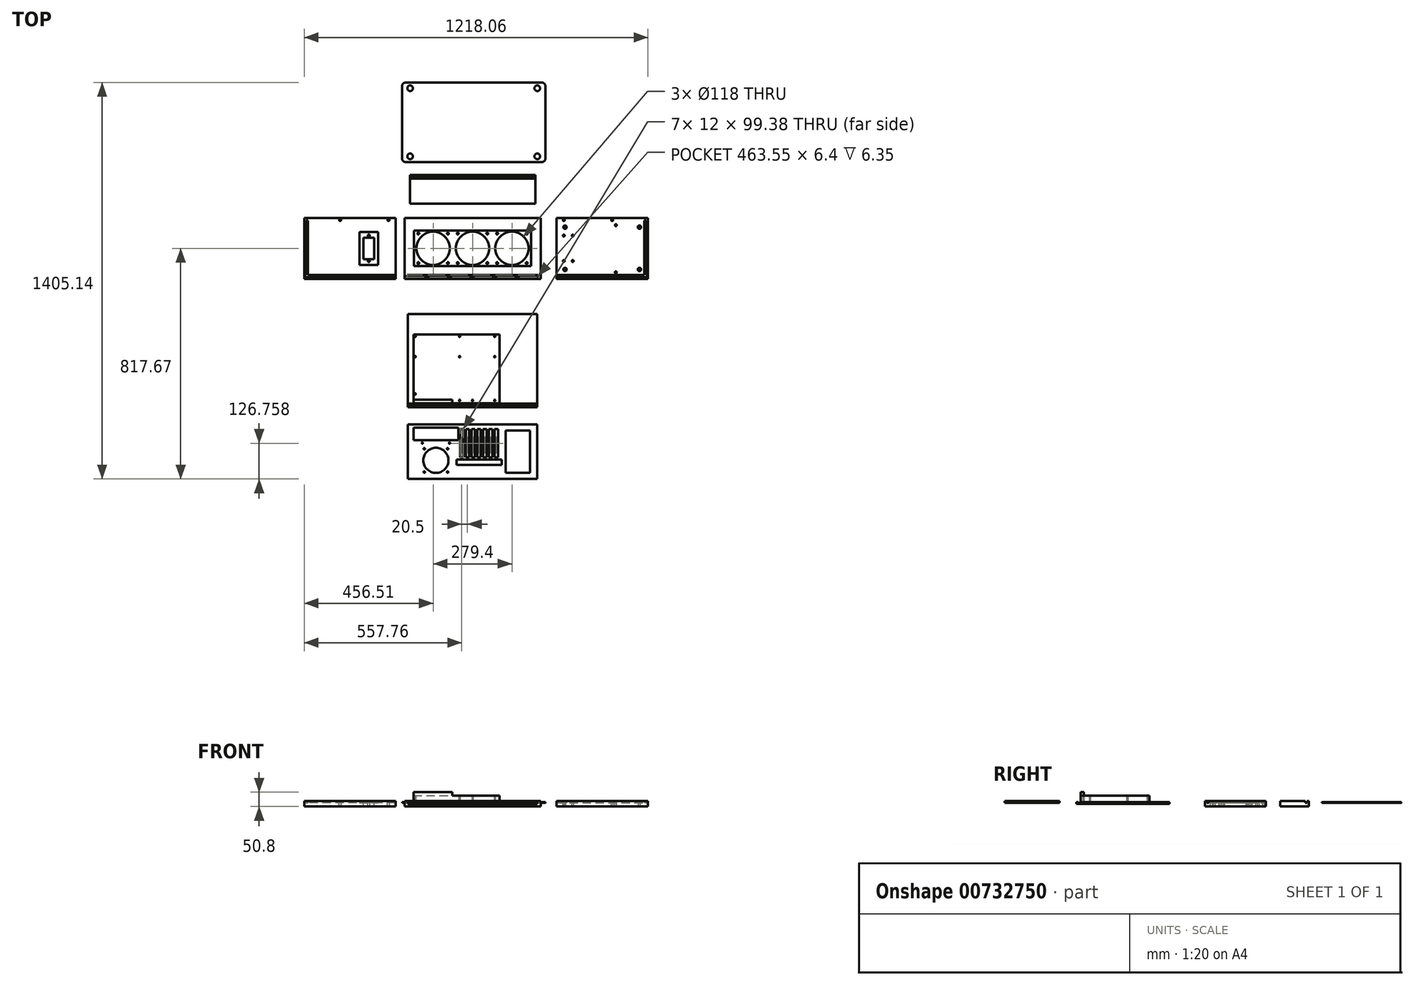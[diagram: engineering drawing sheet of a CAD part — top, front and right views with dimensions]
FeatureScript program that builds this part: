
annotation { "Feature Type Name" : "Feature", "Feature Type Description" : "" }
export const myFeature = defineFeature(function(context is Context, id is Id, definition is map)
    precondition{}
    {
        {
            var Q0;
            Q0=qCreatedBy(makeId("Top.planeOp"),FACE);
            var sketch = newSketch(context, id + "F0", { "sketchPlane" : qUnion([Q0])});
            skLineSegment(sketch, "E0.bottom", {"start": v(241.3, -107.95) * mm, "end": v(-241.3, -107.95) * mm});
            skLineSegment(sketch, "E0.top", {"start": v(241.3, 107.95) * mm, "end": v(-241.3, 107.95) * mm});
            skLineSegment(sketch, "E0.left", {"start": v(241.3, -107.95) * mm, "end": v(241.3, 107.95) * mm});
            skLineSegment(sketch, "E0.right", {"start": v(-241.3, -107.95) * mm, "end": v(-241.3, 107.95) * mm});
            skPoint(sketch, "E0.middle", {"position": v(0, 0) * mm});
            skLineSegment(sketch, "E1.bottom", {"start": v(231.78, -101.6) * mm, "end": v(-231.78, -101.6) * mm});
            skLineSegment(sketch, "E1.top", {"start": v(231.78, -95.2) * mm, "end": v(-231.78, -95.2) * mm});
            skLineSegment(sketch, "E1.left", {"start": v(231.78, -101.6) * mm, "end": v(231.78, -95.2) * mm});
            skLineSegment(sketch, "E1.right", {"start": v(-231.78, -101.6) * mm, "end": v(-231.78, -95.2) * mm});
            skPoint(sketch, "E1.middle", {"position": v(0, -98.4) * mm});
            skCircle(sketch, "E2", {"center": v(139.7, 0) * mm, "radius": 59 * mm});
            skCircle(sketch, "E3", {"center": v(-139.7, 0) * mm, "radius": 59 * mm});
            skCircle(sketch, "E4", {"center": v(0, 0) * mm, "radius": 59 * mm});
            skCircle(sketch, "E5", {"center": v(-192.2, 52.5) * mm, "radius": 3.19 * mm});
            skCircle(sketch, "E6", {"center": v(-192.2, -52.5) * mm, "radius": 3.19 * mm});
            skCircle(sketch, "E7", {"center": v(-87.2, -52.5) * mm, "radius": 3.19 * mm});
            skCircle(sketch, "E8", {"center": v(-87.2, 52.5) * mm, "radius": 3.19 * mm});
            skCircle(sketch, "E9", {"center": v(-52.5, 52.5) * mm, "radius": 3.19 * mm});
            skCircle(sketch, "E10", {"center": v(52.5, 52.5) * mm, "radius": 3.19 * mm});
            skCircle(sketch, "E11", {"center": v(-52.5, -52.5) * mm, "radius": 3.19 * mm});
            skCircle(sketch, "E12", {"center": v(52.5, -52.5) * mm, "radius": 3.19 * mm});
            skCircle(sketch, "E13", {"center": v(87.2, -52.5) * mm, "radius": 3.19 * mm});
            skCircle(sketch, "E14", {"center": v(87.2, 52.5) * mm, "radius": 3.19 * mm});
            skCircle(sketch, "E15", {"center": v(192.2, 52.5) * mm, "radius": 3.19 * mm});
            skCircle(sketch, "E16", {"center": v(192.2, -52.5) * mm, "radius": 3.19 * mm});
            skLineSegment(sketch, "E17.bottom", {"start": v(207.17, -62.5) * mm, "end": v(-207.17, -62.5) * mm});
            skLineSegment(sketch, "E17.top", {"start": v(207.17, 62.5) * mm, "end": v(-207.17, 62.5) * mm});
            skLineSegment(sketch, "E17.left", {"start": v(207.17, -62.5) * mm, "end": v(207.17, 62.5) * mm});
            skLineSegment(sketch, "E17.right", {"start": v(-207.17, -62.5) * mm, "end": v(-207.17, 62.5) * mm});
            skSolve(sketch);
        }
        {
            var Q0;
            Q0=makeQuery(id+"F0.imprint","IMPRINT",FACE,{"disambiguationData":[TD([[makeQuery(id+"F0.imprint","IMPRINT",EDGE,{"derivedFrom":sQuery(id+"F0.wireOp",EDGE,"E1.bottom")}),-1.0]])]});
            var Q1;
            Q1=makeQuery(id+"F0.imprint","IMPRINT",FACE,{"disambiguationData":[TD([[makeQuery(id+"F0.imprint","IMPRINT",EDGE,{"derivedFrom":sQuery(id+"F0.wireOp",EDGE,"E0.bottom")}),-1.0]])]});
            var Q2;
            Q2=makeQuery(id+"F0.imprint","IMPRINT",FACE,{"disambiguationData":[TD([[makeQuery(id+"F0.imprint","IMPRINT",EDGE,{"derivedFrom":sQuery(id+"F0.wireOp",EDGE,"E2")}),-1.0]])]});
            extrude(context, id + "F1", {"entities" : qUnion([Q0, Q1, Q2]), "oppositeDirection" : true, "depth" : 12.7 * mm, "offsetDistance" : 25.4 * mm});
        }
        {
            var Q0;
            Q0=makeQuery(id+"F0.imprint","IMPRINT",FACE,{"disambiguationData":[TD([[makeQuery(id+"F0.imprint","IMPRINT",EDGE,{"derivedFrom":sQuery(id+"F0.wireOp",EDGE,"E0.bottom")}),-1.0]])]});
            extrude(context, id + "F2", {"entities" : qUnion([Q0]), "operationType" : NewBodyOperationType.ADD, "depth" : 6.35 * mm, "offsetDistance" : 25.4 * mm});
        }
        {
            var Q0;
            Q0=qCreatedBy(makeId("Top.planeOp"),FACE);
            var sketch = newSketch(context, id + "F3", { "sketchPlane" : qUnion([Q0])});
            skPoint(sketch, "E18.0", {"position": v(231.78, -95.2) * mm});
            skPoint(sketch, "E18.1", {"position": v(231.78, -101.6) * mm});
            skPoint(sketch, "E18.2", {"position": v(241.3, -107.95) * mm});
            skPoint(sketch, "E18.3", {"position": v(241.3, 107.95) * mm});
            skLineSegment(sketch, "E19.bottom", {"start": v(298, -107.95) * mm, "end": v(621.85, -107.95) * mm});
            skLineSegment(sketch, "E19.top", {"start": v(298, 107.95) * mm, "end": v(621.85, 107.95) * mm});
            skLineSegment(sketch, "E19.left", {"start": v(298, -107.95) * mm, "end": v(298, 107.95) * mm});
            skLineSegment(sketch, "E19.right", {"start": v(621.85, -107.95) * mm, "end": v(621.85, 107.95) * mm});
            skPoint(sketch, "E19.middle", {"position": v(459.93, 0) * mm});
            skLineSegment(sketch, "E20.bottom", {"start": v(294.83, -95.2) * mm, "end": v(625.03, -95.2) * mm});
            skLineSegment(sketch, "E20.top", {"start": v(294.83, -101.6) * mm, "end": v(625.03, -101.6) * mm});
            skLineSegment(sketch, "E20.left", {"start": v(294.83, -95.2) * mm, "end": v(294.83, -101.6) * mm});
            skLineSegment(sketch, "E20.right", {"start": v(625.03, -95.2) * mm, "end": v(625.03, -101.6) * mm});
            skLineSegment(sketch, "E21.bottom", {"start": v(615.5, -97.9) * mm, "end": v(609.13, -97.9) * mm});
            skLineSegment(sketch, "E21.top", {"start": v(615.5, 98.43) * mm, "end": v(609.13, 98.43) * mm});
            skLineSegment(sketch, "E21.left", {"start": v(615.5, -97.9) * mm, "end": v(615.5, 98.43) * mm});
            skLineSegment(sketch, "E21.right", {"start": v(609.13, -97.9) * mm, "end": v(609.13, 98.43) * mm});
            skCircle(sketch, "E22", {"center": v(328, 74.95) * mm, "radius": 3.3 * mm});
            skCircle(sketch, "E23", {"center": v(328, -74.95) * mm, "radius": 3.3 * mm});
            skCircle(sketch, "E24", {"center": v(591.85, -74.95) * mm, "radius": 3.3 * mm});
            skCircle(sketch, "E25", {"center": v(591.85, 74.95) * mm, "radius": 3.3 * mm});
            skCircle(sketch, "E26", {"center": v(328, 74.95) * mm, "radius": 6 * mm});
            skCircle(sketch, "E27", {"center": v(328, -74.95) * mm, "radius": 6 * mm});
            skCircle(sketch, "E28", {"center": v(591.85, 74.95) * mm, "radius": 6 * mm});
            skCircle(sketch, "E29", {"center": v(591.85, -74.95) * mm, "radius": 6 * mm});
            skPoint(sketch, "E30", {"position": v(520.25, -20.34) * mm});
            skCircle(sketch, "E31", {"center": v(494.85, 99.95) * mm, "radius": 3.3 * mm});
            skCircle(sketch, "E32", {"center": v(323.4, 99.95) * mm, "radius": 3.3 * mm});
            skPoint(sketch, "E33.centerSnap0", {"position": v(298, 0) * mm});
            skCircle(sketch, "E34", {"center": v(508.13, 81.95) * mm, "radius": 3.3 * mm});
            skCircle(sketch, "E35", {"center": v(508.13, -85.4) * mm, "radius": 3.3 * mm});
            skLineSegment(sketch, "E36.bottom", {"start": v(355.2, -45.09) * mm, "end": v(323.4, -45.09) * mm});
            skLineSegment(sketch, "E36.top", {"start": v(355.2, 45.08) * mm, "end": v(323.4, 45.08) * mm});
            skLineSegment(sketch, "E36.left", {"start": v(355.2, -45.09) * mm, "end": v(355.2, 45.08) * mm});
            skLineSegment(sketch, "E36.right", {"start": v(323.4, -45.09) * mm, "end": v(323.4, 45.08) * mm});
            skPoint(sketch, "E36.middle", {"position": v(339.3, 0) * mm});
            skCircle(sketch, "E37", {"center": v(323.4, 45.08) * mm, "radius": 3.3 * mm});
            skCircle(sketch, "E38", {"center": v(355.2, 45.08) * mm, "radius": 3.3 * mm});
            skCircle(sketch, "E39", {"center": v(323.4, -45.09) * mm, "radius": 3.3 * mm});
            skCircle(sketch, "E40", {"center": v(355.2, -45.09) * mm, "radius": 3.3 * mm});
            skSolve(sketch);
        }
        {
            var Q0;
            {var subQ0=sQuery(id+"F3.wireOp",EDGE,"E19.left");var subQ1=sQuery(id+"F3.wireOp",EDGE,"E19.top");var subQ2=makeQuery(id+"F3.imprint","INTERSECT",VERTEX,{"derivedFrom":[subQ1,subQ0]});Q0=makeQuery(id+"F3.imprint","IMPRINT",FACE,{"disambiguationData":[TD([[makeQuery(id+"F3.imprint","IMPRINT",EDGE,{"disambiguationData":[TD([[subQ2,-1.0]])],"derivedFrom":subQ1}),-1.0]])]});}
            var Q1;
            {var subQ0=sQuery(id+"F3.wireOp",EDGE,"E21.right");var subQ1=sQuery(id+"F3.wireOp",EDGE,"E19.top");var subQ2=makeQuery(id+"F3.imprint","INTERSECT",VERTEX,{"derivedFrom":[subQ1,subQ0]});Q1=makeQuery(id+"F3.imprint","IMPRINT",FACE,{"disambiguationData":[TD([[makeQuery(id+"F3.imprint","IMPRINT",EDGE,{"disambiguationData":[TD([[subQ2,-1.0]])],"derivedFrom":subQ1}),-1.0]])]});}
            var Q2;
            {var subQ0=sQuery(id+"F3.wireOp",EDGE,"E19.right");var subQ1=sQuery(id+"F3.wireOp",EDGE,"E19.top");var subQ2=makeQuery(id+"F3.imprint","INTERSECT",VERTEX,{"derivedFrom":[subQ1,subQ0]});Q2=makeQuery(id+"F3.imprint","IMPRINT",FACE,{"disambiguationData":[TD([[makeQuery(id+"F3.imprint","IMPRINT",EDGE,{"disambiguationData":[TD([[subQ2,1.0]])],"derivedFrom":subQ1}),-1.0]])]});}
            var Q3;
            {var subQ6=sQuery(id+"F3.wireOp",EDGE,"E21.bottom");Q3=makeQuery(id+"F3.imprint","IMPRINT",FACE,{"disambiguationData":[TD([[makeQuery(id+"F3.imprint","IMPRINT",EDGE,{"derivedFrom":subQ6}),1.0]])]});}
            var Q4;
            {var subQ0=sQuery(id+"F3.wireOp",EDGE,"E19.bottom");Q4=makeQuery(id+"F3.imprint","IMPRINT",FACE,{"disambiguationData":[TD([[makeQuery(id+"F3.imprint","IMPRINT",EDGE,{"derivedFrom":subQ0}),1.0]])]});}
            var Q5;
            {var subQ5=sQuery(id+"F3.wireOp",EDGE,"E21.bottom");Q5=makeQuery(id+"F3.imprint","IMPRINT",FACE,{"disambiguationData":[TD([[makeQuery(id+"F3.imprint","IMPRINT",EDGE,{"derivedFrom":subQ5}),-1.0]])]});}
            var Q6;
            {var subQ5=sQuery(id+"F3.wireOp",EDGE,"E21.top");Q6=makeQuery(id+"F3.imprint","IMPRINT",FACE,{"disambiguationData":[TD([[makeQuery(id+"F3.imprint","IMPRINT",EDGE,{"derivedFrom":subQ5}),1.0]])]});}
            var Q7;
            Q7=makeQuery(id+"F3.imprint","IMPRINT",FACE,{"disambiguationData":[TD([[makeQuery(id+"F3.imprint","IMPRINT",EDGE,{"derivedFrom":sQuery(id+"F3.wireOp",EDGE,"E22")}),-1.0]])]});
            var Q8;
            Q8=makeQuery(id+"F3.imprint","IMPRINT",FACE,{"disambiguationData":[TD([[makeQuery(id+"F3.imprint","IMPRINT",EDGE,{"derivedFrom":sQuery(id+"F3.wireOp",EDGE,"E23")}),-1.0]])]});
            var Q9;
            Q9=makeQuery(id+"F3.imprint","IMPRINT",FACE,{"disambiguationData":[TD([[makeQuery(id+"F3.imprint","IMPRINT",EDGE,{"derivedFrom":sQuery(id+"F3.wireOp",EDGE,"E24")}),-1.0]])]});
            var Q10;
            Q10=makeQuery(id+"F3.imprint","IMPRINT",FACE,{"disambiguationData":[TD([[makeQuery(id+"F3.imprint","IMPRINT",EDGE,{"derivedFrom":sQuery(id+"F3.wireOp",EDGE,"E25")}),-1.0]])]});
            var Q11;
            {var subQ0=sQuery(id+"F3.wireOp",EDGE,"E36.top");var subQ1=sQuery(id+"F3.wireOp",EDGE,"oCOWhfAx-kF6R-myvc-yPfL-ItVIfWdrZVwj");var subQ2=makeQuery(id+"F3.imprint","INTERSECT",VERTEX,{"derivedFrom":[subQ1,subQ0]});Q11=makeQuery(id+"F3.imprint","IMPRINT",FACE,{"disambiguationData":[TD([[makeQuery(id+"F3.imprint","IMPRINT",EDGE,{"disambiguationData":[TD([[subQ2,-1.0]])],"derivedFrom":subQ1}),-1.0]])]});}
            var Q12;
            {var subQ5=sQuery(id+"F3.wireOp",EDGE,"E36.top");var subQ6=sQuery(id+"F3.wireOp",EDGE,"oCOWhfAx-kF6R-myvc-yPfL-ItVIfWdrZVwj");var subQ7=makeQuery(id+"F3.imprint","INTERSECT",VERTEX,{"derivedFrom":[subQ6,subQ5]});Q12=makeQuery(id+"F3.imprint","IMPRINT",FACE,{"disambiguationData":[TD([[makeQuery(id+"F3.imprint","IMPRINT",EDGE,{"disambiguationData":[TD([[subQ7,-1.0]])],"derivedFrom":subQ6}),1.0]])]});}
            var Q13;
            {var subQ5=sQuery(id+"F3.wireOp",EDGE,"E40");var subQ10=sQuery(id+"F3.wireOp",EDGE,"E36.bottom");var subQ11=makeQuery(id+"F3.imprint","INTERSECT",VERTEX,{"derivedFrom":[subQ10,subQ5]});Q13=makeQuery(id+"F3.imprint","IMPRINT",FACE,{"disambiguationData":[TD([[makeQuery(id+"F3.imprint","IMPRINT",EDGE,{"disambiguationData":[TD([[subQ11,-1.0]])],"derivedFrom":subQ10}),-1.0]])]});}
            extrude(context, id + "F4", {"entities" : qUnion([Q0, Q1, Q2, Q3, Q4, Q5, Q6, Q7, Q8, Q9, Q10, Q11, Q12, Q13]), "oppositeDirection" : true, "depth" : 12.7 * mm, "offsetDistance" : 25.4 * mm});
        }
        {
            var Q0;
            {var subQ0=sQuery(id+"F3.wireOp",EDGE,"E19.left");var subQ1=sQuery(id+"F3.wireOp",EDGE,"E19.top");var subQ2=makeQuery(id+"F3.imprint","INTERSECT",VERTEX,{"derivedFrom":[subQ1,subQ0]});Q0=makeQuery(id+"F3.imprint","IMPRINT",FACE,{"disambiguationData":[TD([[makeQuery(id+"F3.imprint","IMPRINT",EDGE,{"disambiguationData":[TD([[subQ2,-1.0]])],"derivedFrom":subQ1}),-1.0]])]});}
            var Q1;
            {var subQ0=sQuery(id+"F3.wireOp",EDGE,"E19.right");var subQ1=sQuery(id+"F3.wireOp",EDGE,"E19.top");var subQ2=makeQuery(id+"F3.imprint","INTERSECT",VERTEX,{"derivedFrom":[subQ1,subQ0]});Q1=makeQuery(id+"F3.imprint","IMPRINT",FACE,{"disambiguationData":[TD([[makeQuery(id+"F3.imprint","IMPRINT",EDGE,{"disambiguationData":[TD([[subQ2,1.0]])],"derivedFrom":subQ1}),-1.0]])]});}
            var Q2;
            {var subQ0=sQuery(id+"F3.wireOp",EDGE,"E19.bottom");Q2=makeQuery(id+"F3.imprint","IMPRINT",FACE,{"disambiguationData":[TD([[makeQuery(id+"F3.imprint","IMPRINT",EDGE,{"derivedFrom":subQ0}),1.0]])]});}
            var Q3;
            {var subQ0=sQuery(id+"F3.wireOp",EDGE,"E36.top");var subQ1=sQuery(id+"F3.wireOp",EDGE,"oCOWhfAx-kF6R-myvc-yPfL-ItVIfWdrZVwj");var subQ2=makeQuery(id+"F3.imprint","INTERSECT",VERTEX,{"derivedFrom":[subQ1,subQ0]});Q3=makeQuery(id+"F3.imprint","IMPRINT",FACE,{"disambiguationData":[TD([[makeQuery(id+"F3.imprint","IMPRINT",EDGE,{"disambiguationData":[TD([[subQ2,-1.0]])],"derivedFrom":subQ1}),-1.0]])]});}
            var Q4;
            {var subQ5=sQuery(id+"F3.wireOp",EDGE,"E36.top");var subQ6=sQuery(id+"F3.wireOp",EDGE,"oCOWhfAx-kF6R-myvc-yPfL-ItVIfWdrZVwj");var subQ7=makeQuery(id+"F3.imprint","INTERSECT",VERTEX,{"derivedFrom":[subQ6,subQ5]});Q4=makeQuery(id+"F3.imprint","IMPRINT",FACE,{"disambiguationData":[TD([[makeQuery(id+"F3.imprint","IMPRINT",EDGE,{"disambiguationData":[TD([[subQ7,-1.0]])],"derivedFrom":subQ6}),1.0]])]});}
            var Q5;
            {var subQ5=sQuery(id+"F3.wireOp",EDGE,"E40");var subQ10=sQuery(id+"F3.wireOp",EDGE,"E36.bottom");var subQ11=makeQuery(id+"F3.imprint","INTERSECT",VERTEX,{"derivedFrom":[subQ10,subQ5]});Q5=makeQuery(id+"F3.imprint","IMPRINT",FACE,{"disambiguationData":[TD([[makeQuery(id+"F3.imprint","IMPRINT",EDGE,{"disambiguationData":[TD([[subQ11,-1.0]])],"derivedFrom":subQ10}),-1.0]])]});}
            extrude(context, id + "F5", {"entities" : qUnion([Q0, Q1, Q2, Q3, Q4, Q5]), "operationType" : NewBodyOperationType.ADD, "depth" : 6.35 * mm, "offsetDistance" : 25.4 * mm});
        }
        {
            var Q0;
            Q0=qCreatedBy(makeId("Top.planeOp"),FACE);
            var sketch = newSketch(context, id + "F6", { "sketchPlane" : qUnion([Q0])});
            skPoint(sketch, "E41.0", {"position": v(-241.3, 107.95) * mm});
            skPoint(sketch, "E41.1", {"position": v(-241.3, -107.95) * mm});
            skPoint(sketch, "E41.2", {"position": v(-231.78, -95.2) * mm});
            skPoint(sketch, "E41.3", {"position": v(-231.78, -101.6) * mm});
            skLineSegment(sketch, "E42.bottom", {"start": v(-272.36, 107.95) * mm, "end": v(-596.2, 107.95) * mm});
            skLineSegment(sketch, "E42.top", {"start": v(-272.36, -107.95) * mm, "end": v(-596.2, -107.95) * mm});
            skLineSegment(sketch, "E42.left", {"start": v(-272.36, 107.95) * mm, "end": v(-272.36, -107.95) * mm});
            skLineSegment(sketch, "E42.right", {"start": v(-596.2, 107.95) * mm, "end": v(-596.2, -107.95) * mm});
            skLineSegment(sketch, "E43.bottom", {"start": v(-269.18, -95.2) * mm, "end": v(-599.38, -95.2) * mm});
            skLineSegment(sketch, "E43.top", {"start": v(-269.18, -101.6) * mm, "end": v(-599.38, -101.6) * mm});
            skLineSegment(sketch, "E43.left", {"start": v(-269.18, -95.2) * mm, "end": v(-269.18, -101.6) * mm});
            skLineSegment(sketch, "E43.right", {"start": v(-599.38, -95.2) * mm, "end": v(-599.38, -101.6) * mm});
            skLineSegment(sketch, "E44.bottom", {"start": v(-348.56, -38.1) * mm, "end": v(-386.66, -38.1) * mm});
            skLineSegment(sketch, "E44.top", {"start": v(-348.56, 38.1) * mm, "end": v(-386.66, 38.1) * mm});
            skLineSegment(sketch, "E44.left", {"start": v(-348.56, -38.1) * mm, "end": v(-348.56, 38.1) * mm});
            skLineSegment(sketch, "E44.right", {"start": v(-386.66, -38.1) * mm, "end": v(-386.66, 38.1) * mm});
            skPoint(sketch, "E44.middle", {"position": v(-367.6, 0) * mm});
            skLineSegment(sketch, "E45.bottom", {"start": v(-589.86, 98.42) * mm, "end": v(-583.48, 98.42) * mm});
            skLineSegment(sketch, "E45.top", {"start": v(-589.86, -99.05) * mm, "end": v(-583.48, -99.05) * mm});
            skLineSegment(sketch, "E45.left", {"start": v(-589.86, 98.42) * mm, "end": v(-589.86, -99.05) * mm});
            skLineSegment(sketch, "E45.right", {"start": v(-583.48, 98.42) * mm, "end": v(-583.48, -99.05) * mm});
            skPoint(sketch, "E46.0", {"position": v(323.4, 99.95) * mm});
            skCircle(sketch, "E47", {"center": v(-297.76, 99.95) * mm, "radius": 3.3 * mm});
            skCircle(sketch, "E48", {"center": v(-469.2, 99.95) * mm, "radius": 3.3 * mm});
            skCircle(sketch, "E49", {"center": v(-367.6, 45.6) * mm, "radius": 3.3 * mm});
            skCircle(sketch, "E50", {"center": v(-367.6, -45.6) * mm, "radius": 3.3 * mm});
            skLineSegment(sketch, "E51.bottom", {"start": v(-400.63, 58.42) * mm, "end": v(-334.59, 58.42) * mm});
            skLineSegment(sketch, "E51.top", {"start": v(-400.63, -58.42) * mm, "end": v(-334.59, -58.42) * mm});
            skLineSegment(sketch, "E51.left", {"start": v(-400.63, 58.42) * mm, "end": v(-400.63, -58.42) * mm});
            skLineSegment(sketch, "E51.right", {"start": v(-334.59, 58.42) * mm, "end": v(-334.59, -58.42) * mm});
            skSolve(sketch);
        }
        {
            var Q0;
            Q0=makeQuery(id+"F6.imprint","IMPRINT",FACE,{"disambiguationData":[TD([[makeQuery(id+"F6.imprint","IMPRINT",EDGE,{"derivedFrom":sQuery(id+"F6.wireOp",EDGE,"E44.bottom")}),1.0]])]});
            var Q1;
            {var subQ0=sQuery(id+"F6.wireOp",EDGE,"E42.top");Q1=makeQuery(id+"F6.imprint","IMPRINT",FACE,{"disambiguationData":[TD([[makeQuery(id+"F6.imprint","IMPRINT",EDGE,{"derivedFrom":subQ0}),-1.0]])]});}
            var Q2;
            {var subQ12=sQuery(id+"F6.wireOp",EDGE,"E45.top");Q2=makeQuery(id+"F6.imprint","IMPRINT",FACE,{"disambiguationData":[TD([[makeQuery(id+"F6.imprint","IMPRINT",EDGE,{"derivedFrom":subQ12}),-1.0]])]});}
            var Q3;
            {var subQ0=sQuery(id+"F6.wireOp",EDGE,"E42.right");var subQ1=sQuery(id+"F6.wireOp",EDGE,"E42.bottom");var subQ2=makeQuery(id+"F6.imprint","INTERSECT",VERTEX,{"derivedFrom":[subQ1,subQ0]});Q3=makeQuery(id+"F6.imprint","IMPRINT",FACE,{"disambiguationData":[TD([[makeQuery(id+"F6.imprint","IMPRINT",EDGE,{"disambiguationData":[TD([[subQ2,1.0]])],"derivedFrom":subQ1}),1.0]])]});}
            var Q4;
            {var subQ0=sQuery(id+"F6.wireOp",EDGE,"E45.right");var subQ1=sQuery(id+"F6.wireOp",EDGE,"E42.bottom");var subQ2=makeQuery(id+"F6.imprint","INTERSECT",VERTEX,{"derivedFrom":[subQ1,subQ0]});Q4=makeQuery(id+"F6.imprint","IMPRINT",FACE,{"disambiguationData":[TD([[makeQuery(id+"F6.imprint","IMPRINT",EDGE,{"disambiguationData":[TD([[subQ2,-1.0]])],"derivedFrom":subQ1}),1.0]])]});}
            var Q5;
            {var subQ5=sQuery(id+"F6.wireOp",EDGE,"E45.top");Q5=makeQuery(id+"F6.imprint","IMPRINT",FACE,{"disambiguationData":[TD([[makeQuery(id+"F6.imprint","IMPRINT",EDGE,{"derivedFrom":subQ5}),1.0]])]});}
            var Q6;
            {var subQ5=sQuery(id+"F6.wireOp",EDGE,"E45.bottom");Q6=makeQuery(id+"F6.imprint","IMPRINT",FACE,{"disambiguationData":[TD([[makeQuery(id+"F6.imprint","IMPRINT",EDGE,{"derivedFrom":subQ5}),-1.0]])]});}
            extrude(context, id + "F7", {"entities" : qUnion([Q0, Q1, Q2, Q3, Q4, Q5, Q6]), "oppositeDirection" : true, "depth" : 12.7 * mm, "offsetDistance" : 25.4 * mm});
        }
        {
            var Q0;
            Q0=makeQuery(id+"F6.imprint","IMPRINT",FACE,{"disambiguationData":[TD([[makeQuery(id+"F6.imprint","IMPRINT",EDGE,{"derivedFrom":sQuery(id+"F6.wireOp",EDGE,"E44.bottom")}),1.0]])]});
            var Q1;
            {var subQ0=sQuery(id+"F6.wireOp",EDGE,"E42.right");var subQ1=sQuery(id+"F6.wireOp",EDGE,"E42.bottom");var subQ2=makeQuery(id+"F6.imprint","INTERSECT",VERTEX,{"derivedFrom":[subQ1,subQ0]});Q1=makeQuery(id+"F6.imprint","IMPRINT",FACE,{"disambiguationData":[TD([[makeQuery(id+"F6.imprint","IMPRINT",EDGE,{"disambiguationData":[TD([[subQ2,1.0]])],"derivedFrom":subQ1}),1.0]])]});}
            var Q2;
            {var subQ0=sQuery(id+"F6.wireOp",EDGE,"E42.top");Q2=makeQuery(id+"F6.imprint","IMPRINT",FACE,{"disambiguationData":[TD([[makeQuery(id+"F6.imprint","IMPRINT",EDGE,{"derivedFrom":subQ0}),-1.0]])]});}
            extrude(context, id + "F8", {"entities" : qUnion([Q0, Q1, Q2]), "operationType" : NewBodyOperationType.ADD, "depth" : 6.35 * mm, "offsetDistance" : 25.4 * mm});
        }
        {
            var Q0;
            Q0=makeQuery(id+"F6.imprint","IMPRINT",FACE,{"disambiguationData":[TD([[makeQuery(id+"F6.imprint","IMPRINT",EDGE,{"derivedFrom":sQuery(id+"F6.wireOp",EDGE,"E44.bottom")}),1.0]])]});
            extrude(context, id + "F9", {"entities" : qUnion([Q0]), "operationType" : NewBodyOperationType.REMOVE, "depth" : 6.35 * mm, "offsetDistance" : 25.4 * mm});
        }
        {
            var Q0;
            Q0=qCreatedBy(makeId("Top.planeOp"),FACE);
            var sketch = newSketch(context, id + "F10", { "sketchPlane" : qUnion([Q0])});
            skLineSegment(sketch, "E52.bottom", {"start": v(95.25, -305.6) * mm, "end": v(95.25, -549.45) * mm});
            skLineSegment(sketch, "E52.top", {"start": v(-209.55, -305.6) * mm, "end": v(-209.55, -549.45) * mm});
            skLineSegment(sketch, "E52.left", {"start": v(95.25, -305.6) * mm, "end": v(-209.55, -305.6) * mm});
            skLineSegment(sketch, "E52.right", {"start": v(95.25, -549.45) * mm, "end": v(-209.55, -549.45) * mm});
            skLineSegment(sketch, "E53.bottom", {"start": v(-71.46, -549.45) * mm, "end": v(-71.46, -536.83) * mm});
            skLineSegment(sketch, "E53.top", {"start": v(-209.55, -549.45) * mm, "end": v(-209.55, -536.83) * mm});
            skLineSegment(sketch, "E53.left", {"start": v(-71.46, -549.45) * mm, "end": v(-209.55, -549.45) * mm});
            skLineSegment(sketch, "E53.right", {"start": v(-71.46, -536.83) * mm, "end": v(-209.55, -536.83) * mm});
            skCircle(sketch, "E54", {"center": v(78.74, -539.29) * mm, "radius": 2.5 * mm});
            skCircle(sketch, "E55", {"center": v(0, -539.29) * mm, "radius": 2.5 * mm});
            skCircle(sketch, "E56", {"center": v(-45.72, -539.29) * mm, "radius": 2.5 * mm});
            skCircle(sketch, "E57", {"center": v(-45.72, -384.35) * mm, "radius": 2.5 * mm});
            skCircle(sketch, "E58", {"center": v(78.74, -384.35) * mm, "radius": 2.5 * mm});
            skCircle(sketch, "E59", {"center": v(-45.72, -311.96) * mm, "radius": 2.5 * mm});
            skCircle(sketch, "E60", {"center": v(78.74, -311.96) * mm, "radius": 2.5 * mm});
            skCircle(sketch, "E61", {"center": v(-203.2, -311.96) * mm, "radius": 2.5 * mm});
            skCircle(sketch, "E62", {"center": v(-203.2, -384.35) * mm, "radius": 2.5 * mm});
            skCircle(sketch, "E63", {"center": v(-203.2, -516.43) * mm, "radius": 2.5 * mm});
            skSolve(sketch);
        }
        {
            var Q0;
            Q0=makeQuery(id+"F10.imprint","IMPRINT",FACE,{"disambiguationData":[TD([[makeQuery(id+"F10.imprint","IMPRINT",EDGE,{"derivedFrom":sQuery(id+"F10.wireOp",EDGE,"E52.bottom")}),-1.0]])]});
            var Q1;
            Q1=makeQuery(id+"F10.imprint","IMPRINT",FACE,{"disambiguationData":[TD([[makeQuery(id+"F10.imprint","IMPRINT",EDGE,{"derivedFrom":sQuery(id+"F10.wireOp",EDGE,"E53.bottom")}),1.0]])]});
            extrude(context, id + "F11", {"entities" : qUnion([Q0, Q1]), "depth" : 25.4 * mm, "offsetDistance" : 25.4 * mm});
        }
        {
            var Q0;
            Q0=makeQuery(id+"F10.imprint","IMPRINT",FACE,{"disambiguationData":[TD([[makeQuery(id+"F10.imprint","IMPRINT",EDGE,{"derivedFrom":sQuery(id+"F10.wireOp",EDGE,"E53.bottom")}),1.0]])]});
            extrude(context, id + "F12", {"entities" : qUnion([Q0]), "operationType" : NewBodyOperationType.ADD, "depth" : 38.1 * mm, "offsetDistance" : 25.4 * mm});
        }
        {
            var Q0;
            Q0=qCreatedBy(makeId("Top.planeOp"),FACE);
            var sketch = newSketch(context, id + "F13", { "sketchPlane" : qUnion([Q0])});
            skLineSegment(sketch, "E64.bottom", {"start": v(228.6, -563.67) * mm, "end": v(-228.6, -563.67) * mm});
            skLineSegment(sketch, "E64.top", {"start": v(228.6, -233.47) * mm, "end": v(-228.6, -233.47) * mm});
            skLineSegment(sketch, "E64.left", {"start": v(228.6, -563.67) * mm, "end": v(228.6, -233.47) * mm});
            skLineSegment(sketch, "E64.right", {"start": v(-228.6, -563.67) * mm, "end": v(-228.6, -233.47) * mm});
            skPoint(sketch, "E65.0", {"position": v(-241.3, -107.95) * mm});
            skPoint(sketch, "E65.1", {"position": v(241.3, -107.95) * mm});
            skLineSegment(sketch, "E66.bottom", {"start": v(269.88, -557.32) * mm, "end": v(-231.77, -557.32) * mm});
            skLineSegment(sketch, "E66.top", {"start": v(269.88, -550.95) * mm, "end": v(-231.77, -550.95) * mm});
            skLineSegment(sketch, "E66.left", {"start": v(269.88, -557.32) * mm, "end": v(269.88, -550.95) * mm});
            skLineSegment(sketch, "E66.right", {"start": v(-231.77, -557.32) * mm, "end": v(-231.77, -550.95) * mm});
            skSolve(sketch);
        }
        {
            var Q0;
            {var subQ0=sQuery(id+"F13.wireOp",EDGE,"E64.top");Q0=makeQuery(id+"F13.imprint","IMPRINT",FACE,{"disambiguationData":[TD([[makeQuery(id+"F13.imprint","IMPRINT",EDGE,{"derivedFrom":subQ0}),1.0]])]});}
            var Q1;
            {var subQ0=sQuery(id+"F13.wireOp",EDGE,"E66.bottom");var subQ1=sQuery(id+"F13.wireOp",EDGE,"E64.left");var subQ2=makeQuery(id+"F13.imprint","INTERSECT",VERTEX,{"derivedFrom":[subQ1,subQ0]});Q1=makeQuery(id+"F13.imprint","IMPRINT",FACE,{"disambiguationData":[TD([[makeQuery(id+"F13.imprint","IMPRINT",EDGE,{"disambiguationData":[TD([[subQ2,-1.0]])],"derivedFrom":subQ1}),1.0]])]});}
            var Q2;
            {var subQ0=sQuery(id+"F13.wireOp",EDGE,"E64.bottom");Q2=makeQuery(id+"F13.imprint","IMPRINT",FACE,{"disambiguationData":[TD([[makeQuery(id+"F13.imprint","IMPRINT",EDGE,{"derivedFrom":subQ0}),-1.0]])]});}
            extrude(context, id + "F14", {"entities" : qUnion([Q0, Q1, Q2]), "oppositeDirection" : true, "depth" : 3.2 * mm, "offsetDistance" : 25.4 * mm});
        }
        {
            var Q0;
            {var subQ0=sQuery(id+"F13.wireOp",EDGE,"E64.top");Q0=makeQuery(id+"F13.imprint","IMPRINT",FACE,{"disambiguationData":[TD([[makeQuery(id+"F13.imprint","IMPRINT",EDGE,{"derivedFrom":subQ0}),1.0]])]});}
            var Q1;
            {var subQ0=sQuery(id+"F13.wireOp",EDGE,"E64.bottom");Q1=makeQuery(id+"F13.imprint","IMPRINT",FACE,{"disambiguationData":[TD([[makeQuery(id+"F13.imprint","IMPRINT",EDGE,{"derivedFrom":subQ0}),-1.0]])]});}
            extrude(context, id + "F15", {"entities" : qUnion([Q0, Q1]), "operationType" : NewBodyOperationType.ADD, "depth" : 3.2 * mm, "offsetDistance" : 25.4 * mm});
        }
        {
            var Q0;
            Q0=qCreatedBy(makeId("Top.planeOp"),FACE);
            var sketch = newSketch(context, id + "F16", { "sketchPlane" : qUnion([Q0])});
            skPoint(sketch, "E67.0", {"position": v(-228.6, -563.67) * mm});
            skPoint(sketch, "E67.1", {"position": v(228.6, -563.67) * mm});
            skLineSegment(sketch, "E68.MirrorCS", {"start": v(29.05, -641.22) * mm, "end": v(17.05, -641.22) * mm});
            skLineSegment(sketch, "E69.MirrorCS", {"start": v(8.55, -641.22) * mm, "end": v(-3.45, -641.22) * mm});
            skLineSegment(sketch, "E70.MirrorCS", {"start": v(70.05, -641.22) * mm, "end": v(58.05, -641.22) * mm});
            skLineSegment(sketch, "E71.MirrorCS", {"start": v(-11.95, -641.22) * mm, "end": v(-23.95, -641.22) * mm});
            skLineSegment(sketch, "E72.MirrorCS", {"start": v(49.55, -641.22) * mm, "end": v(37.55, -641.22) * mm});
            skLineSegment(sketch, "E73.MirrorCS", {"start": v(29.05, -740.6) * mm, "end": v(17.05, -740.6) * mm});
            skLineSegment(sketch, "E74.MirrorCS", {"start": v(90.55, -740.6) * mm, "end": v(78.55, -740.6) * mm});
            skLineSegment(sketch, "E75.MirrorCS", {"start": v(8.55, -740.6) * mm, "end": v(-3.45, -740.6) * mm});
            skLineSegment(sketch, "E76.MirrorCS", {"start": v(49.55, -740.6) * mm, "end": v(37.55, -740.6) * mm});
            skLineSegment(sketch, "E77.MirrorCS", {"start": v(90.55, -641.22) * mm, "end": v(78.55, -641.22) * mm});
            skLineSegment(sketch, "E78.MirrorCS", {"start": v(-32.45, -740.6) * mm, "end": v(-44.45, -740.6) * mm});
            skLineSegment(sketch, "E79.MirrorCS", {"start": v(-11.95, -740.6) * mm, "end": v(-23.95, -740.6) * mm});
            skLineSegment(sketch, "E80.MirrorCS", {"start": v(70.05, -740.6) * mm, "end": v(58.05, -740.6) * mm});
            skLineSegment(sketch, "E81.MirrorCS", {"start": v(-32.45, -641.22) * mm, "end": v(-44.45, -641.22) * mm});
            skLineSegment(sketch, "E82.MirrorCS", {"start": v(-57.15, -748.22) * mm, "end": v(-57.15, -768.22) * mm});
            skLineSegment(sketch, "E83.MirrorCS", {"start": v(-57.15, -748.22) * mm, "end": v(103.25, -748.22) * mm});
            skLineSegment(sketch, "E84.MirrorCS", {"start": v(103.25, -748.22) * mm, "end": v(103.25, -768.22) * mm});
            skLineSegment(sketch, "E85.MirrorCS", {"start": v(-11.95, -740.6) * mm, "end": v(-11.95, -641.22) * mm});
            skLineSegment(sketch, "E86.MirrorCS", {"start": v(70.05, -740.6) * mm, "end": v(70.05, -641.22) * mm});
            skLineSegment(sketch, "E87.MirrorCS", {"start": v(8.55, -740.6) * mm, "end": v(8.55, -641.22) * mm});
            skLineSegment(sketch, "E88.MirrorCS", {"start": v(90.55, -740.6) * mm, "end": v(90.55, -641.22) * mm});
            skLineSegment(sketch, "E89.MirrorCS", {"start": v(17.05, -641.22) * mm, "end": v(17.05, -740.6) * mm});
            skLineSegment(sketch, "E90.MirrorCS", {"start": v(103.25, -768.22) * mm, "end": v(-57.15, -768.22) * mm});
            skLineSegment(sketch, "E91.MirrorCS", {"start": v(-32.45, -740.6) * mm, "end": v(-32.45, -641.22) * mm});
            skLineSegment(sketch, "E92.MirrorCS", {"start": v(-3.45, -740.6) * mm, "end": v(-3.45, -641.22) * mm});
            skLineSegment(sketch, "E93.MirrorCS", {"start": v(49.55, -740.6) * mm, "end": v(49.55, -641.22) * mm});
            skLineSegment(sketch, "E94.MirrorCS", {"start": v(78.55, -740.6) * mm, "end": v(78.55, -641.22) * mm});
            skLineSegment(sketch, "E95.MirrorCS", {"start": v(228.6, -817.67) * mm, "end": v(228.6, -624.02) * mm});
            skLineSegment(sketch, "E96.MirrorCS", {"start": v(-228.6, -817.67) * mm, "end": v(-228.6, -624.02) * mm});
            skLineSegment(sketch, "E97.MirrorCS", {"start": v(29.05, -641.22) * mm, "end": v(29.05, -740.6) * mm});
            skLineSegment(sketch, "E98.MirrorCS", {"start": v(228.6, -817.67) * mm, "end": v(-228.6, -817.67) * mm});
            skLineSegment(sketch, "E99.MirrorCS", {"start": v(228.6, -624.02) * mm, "end": v(-228.6, -624.02) * mm});
            skLineSegment(sketch, "E100.MirrorCS", {"start": v(58.05, -740.6) * mm, "end": v(58.05, -641.22) * mm});
            skLineSegment(sketch, "E101.MirrorCS", {"start": v(-23.95, -740.6) * mm, "end": v(-23.95, -641.22) * mm});
            skLineSegment(sketch, "E102.MirrorCS", {"start": v(37.55, -740.6) * mm, "end": v(37.55, -641.22) * mm});
            skLineSegment(sketch, "E103.MirrorCS", {"start": v(-44.45, -740.6) * mm, "end": v(-44.45, -641.22) * mm});
            skLineSegment(sketch, "E104.bottom", {"start": v(-209.2, -635.22) * mm, "end": v(-50.45, -635.22) * mm});
            skLineSegment(sketch, "E104.top", {"start": v(-209.2, -679.67) * mm, "end": v(-50.45, -679.67) * mm});
            skLineSegment(sketch, "E104.left", {"start": v(-209.2, -635.22) * mm, "end": v(-209.2, -679.67) * mm});
            skLineSegment(sketch, "E104.right", {"start": v(-50.45, -635.22) * mm, "end": v(-50.45, -679.67) * mm});
            skLineSegment(sketch, "E105.bottom", {"start": v(203.2, -795.85) * mm, "end": v(117.2, -795.85) * mm});
            skLineSegment(sketch, "E105.top", {"start": v(203.2, -645.85) * mm, "end": v(117.2, -645.85) * mm});
            skLineSegment(sketch, "E105.left", {"start": v(203.2, -795.85) * mm, "end": v(203.2, -645.85) * mm});
            skLineSegment(sketch, "E105.right", {"start": v(117.2, -795.85) * mm, "end": v(117.2, -645.85) * mm});
            skPoint(sketch, "E105.middle", {"position": v(160.2, -720.85) * mm});
            skPoint(sketch, "E105.middle.positionSnap0", {"position": v(228.6, -720.85) * mm});
            skPoint(sketch, "E105.centerSnap0", {"position": v(228.6, -720.85) * mm});
            skCircle(sketch, "E106", {"center": v(-129.82, -751.63) * mm, "radius": 44.5 * mm});
            skCircle(sketch, "E107", {"center": v(-171.07, -710.38) * mm, "radius": 2.5 * mm});
            skCircle(sketch, "E108", {"center": v(-88.57, -710.38) * mm, "radius": 2.5 * mm});
            skCircle(sketch, "E109", {"center": v(-171.07, -792.88) * mm, "radius": 2.5 * mm});
            skCircle(sketch, "E110", {"center": v(-88.57, -792.88) * mm, "radius": 2.5 * mm});
            skCircle(sketch, "E111", {"center": v(-177.93, -690.17) * mm, "radius": 2.1 * mm});
            skCircle(sketch, "E112", {"center": v(-81.73, -690.17) * mm, "radius": 2.18 * mm});
            skSolve(sketch);
        }
        {
            var Q0;
            Q0=makeQuery(id+"F16.imprint","IMPRINT",FACE,{"disambiguationData":[TD([[makeQuery(id+"F16.imprint","IMPRINT",EDGE,{"derivedFrom":sQuery(id+"F16.wireOp",EDGE,"eNknI9Zd-MtiG-OOVb-QZow-ef8niGClEtnW.bottom")}),1.0]])]});
            var Q1;
            Q1=makeQuery(id+"F16.imprint","IMPRINT",FACE,{"disambiguationData":[TD([[makeQuery(id+"F16.imprint","IMPRINT",EDGE,{"derivedFrom":sQuery(id+"F16.wireOp",EDGE,"E68.MirrorCS")}),-1.0]])]});
            extrude(context, id + "F17", {"entities" : qUnion([Q0, Q1]), "depth" : 6.38 * mm, "offsetDistance" : 25.4 * mm});
        }
        {
            var Q0;
            Q0=qCreatedBy(makeId("Top.planeOp"),FACE);
            var sketch = newSketch(context, id + "F18", { "sketchPlane" : qUnion([Q0])});
            skPoint(sketch, "E113.0", {"position": v(-241.3, 107.95) * mm});
            skPoint(sketch, "E113.1", {"position": v(241.3, 107.95) * mm});
            skPoint(sketch, "E113.2", {"position": v(-231.78, -95.2) * mm});
            skPoint(sketch, "E113.3", {"position": v(231.78, -95.2) * mm});
            skLineSegment(sketch, "E114.bottom", {"start": v(222.25, 158.75) * mm, "end": v(-222.25, 158.75) * mm});
            skLineSegment(sketch, "E114.top", {"start": v(222.25, 260.35) * mm, "end": v(-222.25, 260.35) * mm});
            skLineSegment(sketch, "E114.left", {"start": v(222.25, 158.75) * mm, "end": v(222.25, 260.35) * mm});
            skLineSegment(sketch, "E114.right", {"start": v(-222.25, 158.75) * mm, "end": v(-222.25, 260.35) * mm});
            skPoint(sketch, "E114.middle", {"position": v(0, 209.55) * mm});
            skLineSegment(sketch, "E115.bottom", {"start": v(225.43, 247.62) * mm, "end": v(-225.43, 247.62) * mm});
            skLineSegment(sketch, "E115.top", {"start": v(225.43, 254) * mm, "end": v(-225.43, 254) * mm});
            skLineSegment(sketch, "E115.left", {"start": v(225.43, 247.62) * mm, "end": v(225.43, 254) * mm});
            skLineSegment(sketch, "E115.right", {"start": v(-225.43, 247.62) * mm, "end": v(-225.43, 254) * mm});
            skPoint(sketch, "E115.middle", {"position": v(0, 250.81) * mm});
            skSolve(sketch);
        }
        {
            var Q0;
            {var subQ0=sQuery(id+"F18.wireOp",EDGE,"E114.bottom");Q0=makeQuery(id+"F18.imprint","IMPRINT",FACE,{"disambiguationData":[TD([[makeQuery(id+"F18.imprint","IMPRINT",EDGE,{"derivedFrom":subQ0}),-1.0]])]});}
            var Q1;
            {var subQ0=sQuery(id+"F18.wireOp",EDGE,"E115.bottom");var subQ1=sQuery(id+"F18.wireOp",EDGE,"E114.left");var subQ2=makeQuery(id+"F18.imprint","INTERSECT",VERTEX,{"derivedFrom":[subQ1,subQ0]});Q1=makeQuery(id+"F18.imprint","IMPRINT",FACE,{"disambiguationData":[TD([[makeQuery(id+"F18.imprint","IMPRINT",EDGE,{"disambiguationData":[TD([[subQ2,-1.0]])],"derivedFrom":subQ1}),1.0]])]});}
            var Q2;
            {var subQ0=sQuery(id+"F18.wireOp",EDGE,"E114.top");Q2=makeQuery(id+"F18.imprint","IMPRINT",FACE,{"disambiguationData":[TD([[makeQuery(id+"F18.imprint","IMPRINT",EDGE,{"derivedFrom":subQ0}),1.0]])]});}
            extrude(context, id + "F19", {"entities" : qUnion([Q0, Q1, Q2]), "oppositeDirection" : true, "depth" : 12.7 * mm, "offsetDistance" : 25.4 * mm});
        }
        {
            var Q0;
            {var subQ0=sQuery(id+"F18.wireOp",EDGE,"E114.top");Q0=makeQuery(id+"F18.imprint","IMPRINT",FACE,{"disambiguationData":[TD([[makeQuery(id+"F18.imprint","IMPRINT",EDGE,{"derivedFrom":subQ0}),1.0]])]});}
            var Q1;
            {var subQ0=sQuery(id+"F18.wireOp",EDGE,"E114.bottom");Q1=makeQuery(id+"F18.imprint","IMPRINT",FACE,{"disambiguationData":[TD([[makeQuery(id+"F18.imprint","IMPRINT",EDGE,{"derivedFrom":subQ0}),-1.0]])]});}
            extrude(context, id + "F20", {"entities" : qUnion([Q0, Q1]), "operationType" : NewBodyOperationType.ADD, "depth" : 6.35 * mm, "offsetDistance" : 25.4 * mm});
        }
        {
            var Q0;
            Q0=qCreatedBy(makeId("Top.planeOp"),FACE);
            var sketch = newSketch(context, id + "F21", { "sketchPlane" : qUnion([Q0])});
            skLineSegment(sketch, "E116.bottom", {"start": v(-237.03, 305.53) * mm, "end": v(245.57, 305.53) * mm});
            skLineSegment(sketch, "E116.top", {"start": v(-237.03, 587.47) * mm, "end": v(245.57, 587.47) * mm});
            skLineSegment(sketch, "E116.left", {"start": v(-249.73, 318.23) * mm, "end": v(-249.73, 574.77) * mm});
            skLineSegment(sketch, "E116.right", {"start": v(258.27, 318.23) * mm, "end": v(258.27, 574.77) * mm});
            skCircle(sketch, "E117", {"center": v(-221.08, 567.15) * mm, "radius": 10 * mm});
            skCircle(sketch, "E118", {"center": v(-221.08, 325.85) * mm, "radius": 10 * mm});
            skCircle(sketch, "E119", {"center": v(229.62, 567.15) * mm, "radius": 10 * mm});
            skCircle(sketch, "E120", {"center": v(229.62, 325.85) * mm, "radius": 10 * mm});
            skPoint(sketch, "E121.visualSharp", {"position": v(-249.73, 587.47) * mm});
            skArc(sketch, "E121.filletArc", {"start": v(-237.03, 587.47) * mm, "mid": v(-246.01, 583.75) * mm, "end": v(-249.73, 574.77) * mm});
            skPoint(sketch, "E122.visualSharp", {"position": v(258.27, 587.47) * mm});
            skArc(sketch, "E122.filletArc", {"start": v(258.27, 574.77) * mm, "mid": v(254.55, 583.75) * mm, "end": v(245.57, 587.47) * mm});
            skPoint(sketch, "E123.visualSharp", {"position": v(-249.73, 305.53) * mm});
            skArc(sketch, "E123.filletArc", {"start": v(-249.73, 318.23) * mm, "mid": v(-246.01, 309.25) * mm, "end": v(-237.03, 305.53) * mm});
            skPoint(sketch, "E124.visualSharp", {"position": v(258.27, 305.53) * mm});
            skArc(sketch, "E124.filletArc", {"start": v(245.57, 305.53) * mm, "mid": v(254.55, 309.25) * mm, "end": v(258.27, 318.23) * mm});
            skPoint(sketch, "E125", {"position": v(-249.73, 446.5) * mm});
            skPoint(sketch, "E126", {"position": v(258.27, 446.5) * mm});
            skPoint(sketch, "E127", {"position": v(4.27, 587.47) * mm});
            skPoint(sketch, "E128", {"position": v(4.27, 305.53) * mm});
            skSolve(sketch);
        }
        {
            var Q0;
            Q0=makeQuery(id+"F21.imprint","IMPRINT",FACE,{"disambiguationData":[TD([[makeQuery(id+"F21.imprint","IMPRINT",EDGE,{"derivedFrom":sQuery(id+"F21.wireOp",EDGE,"E116.bottom")}),1.0]])]});
            extrude(context, id + "F22", {"entities" : qUnion([Q0]), "depth" : 3 * mm, "offsetDistance" : 25.4 * mm});
        }
    });
